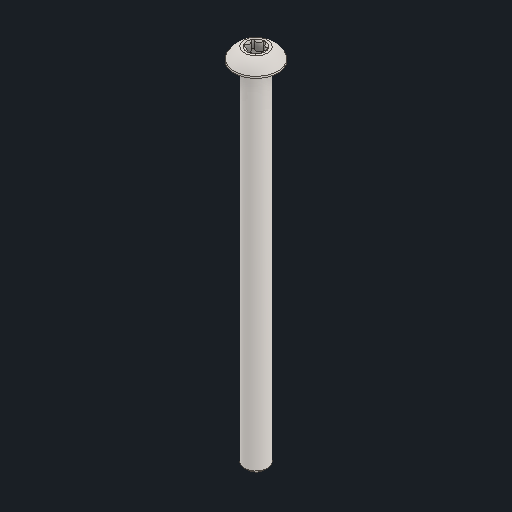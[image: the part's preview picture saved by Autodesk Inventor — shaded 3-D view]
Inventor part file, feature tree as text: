
AUTODESK INVENTOR PART (.ipt)
format: ipt  version: 2024 (Build 280153000, 153)  size: 143,360 bytes
history: native  units: in
note: dims shown in document units (in); Inventor stores cm internally (conversion verified against a paired STEP export)
features: chamfer x1
ambient origin geometry x8: Origin, YZ Plane, XZ Plane, XY Plane, X Axis, Y Axis, Z Axis, Center Point
bodies: Solid1 (feature_tree)
feature tree (1):
  chamfer  "Chamfer2"  [1 undecoded]
note: 1 required parameter value undecoded (feature->parameter linkage not recoverable at this tier; creation-order binding heuristic only, values carry confidence <= 0.55)
